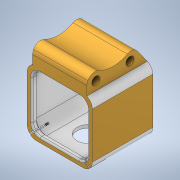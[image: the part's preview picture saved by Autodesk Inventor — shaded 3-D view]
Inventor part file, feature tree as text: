
AUTODESK INVENTOR PART (.ipt)
format: ipt  version: 2020 (Build 240168000, 168)  size: 285,184 bytes
history: native  units: in
note: dims shown in document units (in); Inventor stores cm internally (conversion verified against a paired STEP export)
features: extrude x4, sketch x4, other x3, projected_geometry x3, fillet x2
ambient origin geometry x8: Origin, YZ Plane, XZ Plane, XY Plane, X Axis, Y Axis, Z Axis, Center Point
bodies: Solid1 (feature_tree)
feature tree (16):
  other  "Assembly4.iam"
  other  "Kauri modular session 5 mount.ipt:1"
  other  "session 5.ipt:1"
  extrude  "Extrusion1"  Depth=0.3937in TaperAngle=0.0deg
  extrude  "Extrusion2"  Depth=1.0in TaperAngle=0.0deg
  extrude  "Extrusion3"  Depth=0.3937in TaperAngle=0.0deg
  fillet  "Fillet1"  Radius=0.2362in
  fillet  "Fillet2"  Radius=0.0394in
  extrude  "Extrusion4"  Depth=0.3937in
  sketch  "Sketch1"  dims[d0=0.3937in d1=1.0in d2=0.0in]
  projected_geometry  "Projected Loop1"
  sketch  "Sketch2"  dims[d3=0.5906in d4=1.0in d5=0.0in]
  sketch  "Sketch3"  dims[d6=0.9843in d7=0.3937in d8=0.0in d9=0.2362in d10=0.0394in]
  projected_geometry  "Projected Loop2"
  sketch  "Sketch4"  dims[d12=0.0197in d15=0.3937in d16=0.0in d17=0.0197in d18=0.0197in d19=0.0197in d20=0.0197in]
  projected_geometry  "Projected Loop3"
